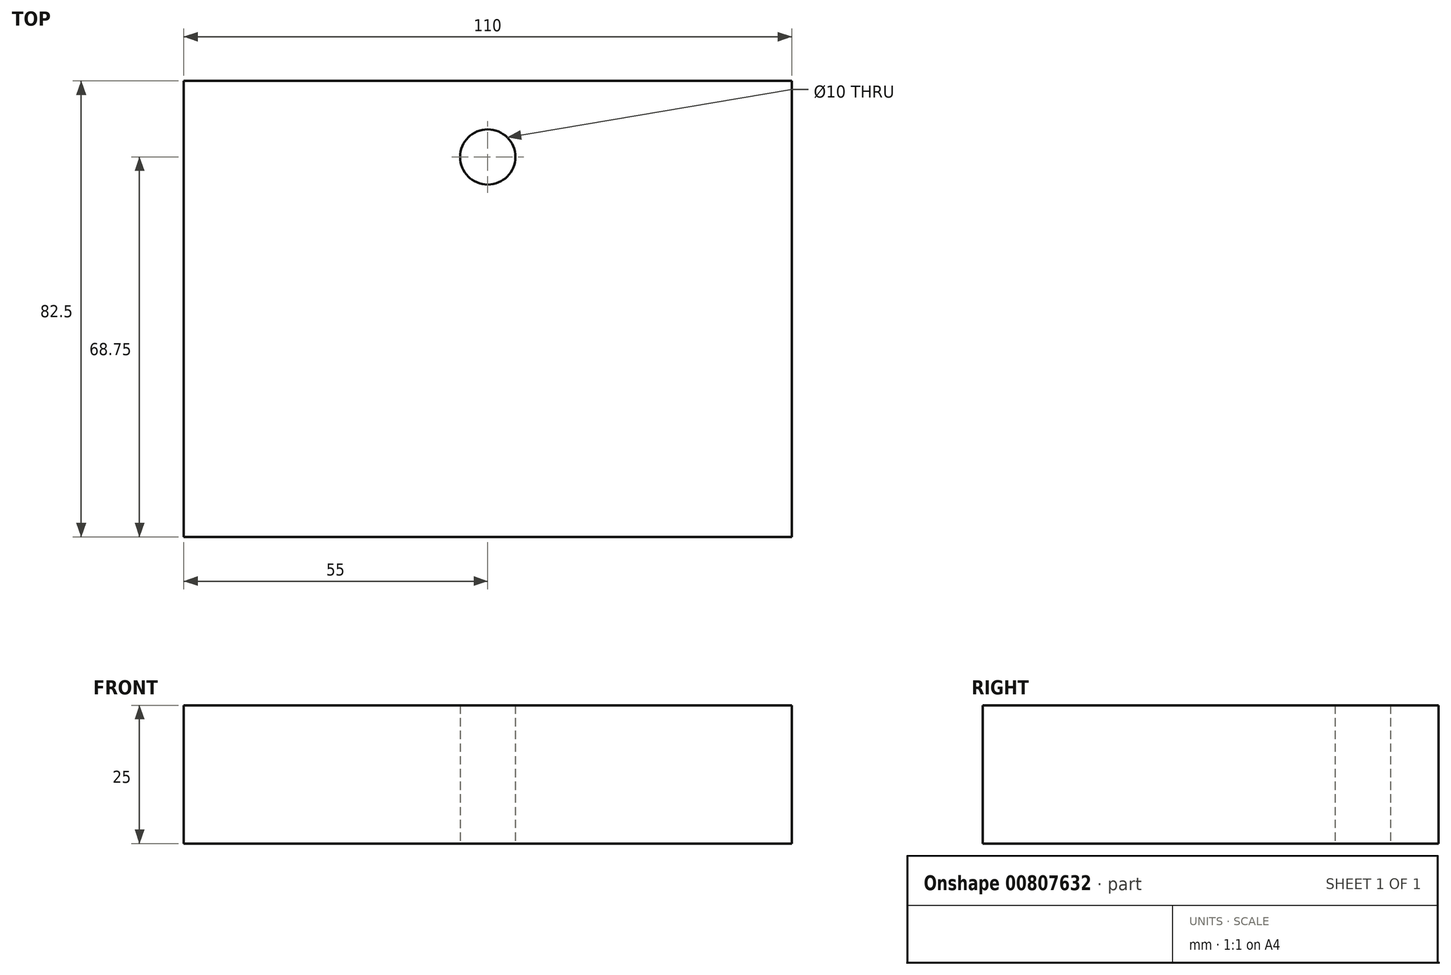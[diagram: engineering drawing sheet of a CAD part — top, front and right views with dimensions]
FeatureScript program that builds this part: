
annotation { "Feature Type Name" : "Feature", "Feature Type Description" : "" }
export const myFeature = defineFeature(function(context is Context, id is Id, definition is map)
    precondition{}
    {
        {
            var Q0;
            Q0=qCreatedBy(makeId("Top.planeOp"),FACE);
            var sketch = newSketch(context, id + "F0", { "sketchPlane" : qUnion([Q0])});
            skLineSegment(sketch, "E0.bottom", {"start": v(55, 41.25) * mm, "end": v(-55, 41.25) * mm});
            skLineSegment(sketch, "E0.top", {"start": v(55, -41.25) * mm, "end": v(-55, -41.25) * mm});
            skLineSegment(sketch, "E0.left", {"start": v(55, 41.25) * mm, "end": v(55, -41.25) * mm});
            skLineSegment(sketch, "E0.right", {"start": v(-55, 41.25) * mm, "end": v(-55, -41.25) * mm});
            skPoint(sketch, "E0.middle", {"position": v(0, 0) * mm});
            skCircle(sketch, "E1", {"center": v(0, 0) * mm, "radius": 27.5 * mm, "construction": true});
            skSolve(sketch);
        }
        {
            var Q0;
            Q0 = qSketchRegion(id + "F0", true);
            extrude(context, id + "F1", {"entities" : qUnion([Q0]), "depth" : 25 * mm, "offsetDistance" : 25 * mm});
        }
        {
            var Q0;
            Q0=makeQuery(id+"F1.opExtrude","CAP_FACE",FACE,{"disambiguationData":[OSD([sQuery(id+"F0.wireOp",EDGE,"E0.bottom"),sQuery(id+"F0.wireOp",EDGE,"E0.top"),sQuery(id+"F0.wireOp",EDGE,"E0.left"),sQuery(id+"F0.wireOp",EDGE,"E0.right")])],"isStart":false});
            var sketch = newSketch(context, id + "F2", { "sketchPlane" : qUnion([Q0])});
            skCircle(sketch, "E2.0", {"center": v(0, 0) * mm, "radius": 27.5 * mm, "construction": true});
            skPoint(sketch, "E3", {"position": v(0, 27.5) * mm});
            skSolve(sketch);
        }
        {
            var Q0;
            Q0=sQuery(id+"F2.wireOp",VERTEX,"E3");
            var Q1;
            Q1=makeQuery(id+"F1.opExtrude","SWEPT_BODY",BODY,{"disambiguationData":[OSD([sQuery(id+"F0.wireOp",EDGE,"E0.bottom"),sQuery(id+"F0.wireOp",EDGE,"E0.top"),sQuery(id+"F0.wireOp",EDGE,"E0.left"),sQuery(id+"F0.wireOp",EDGE,"E0.right")])]});
            hole(context, id + "F3", {"style" : HoleStyle.SIMPLE, "endStyle" : HoleEndStyle.THROUGH, "holeDiameter" : 10 * mm, "majorDiameter" : 5 * mm, "isTappedThrough" : true, "tappedDepth" : 12 * mm, "tapClearance" : 3, "locations" : qUnion([Q0]), "scope" : qUnion([Q1]), "startStyle" : HoleStartStyle.PART});
        }
    });
